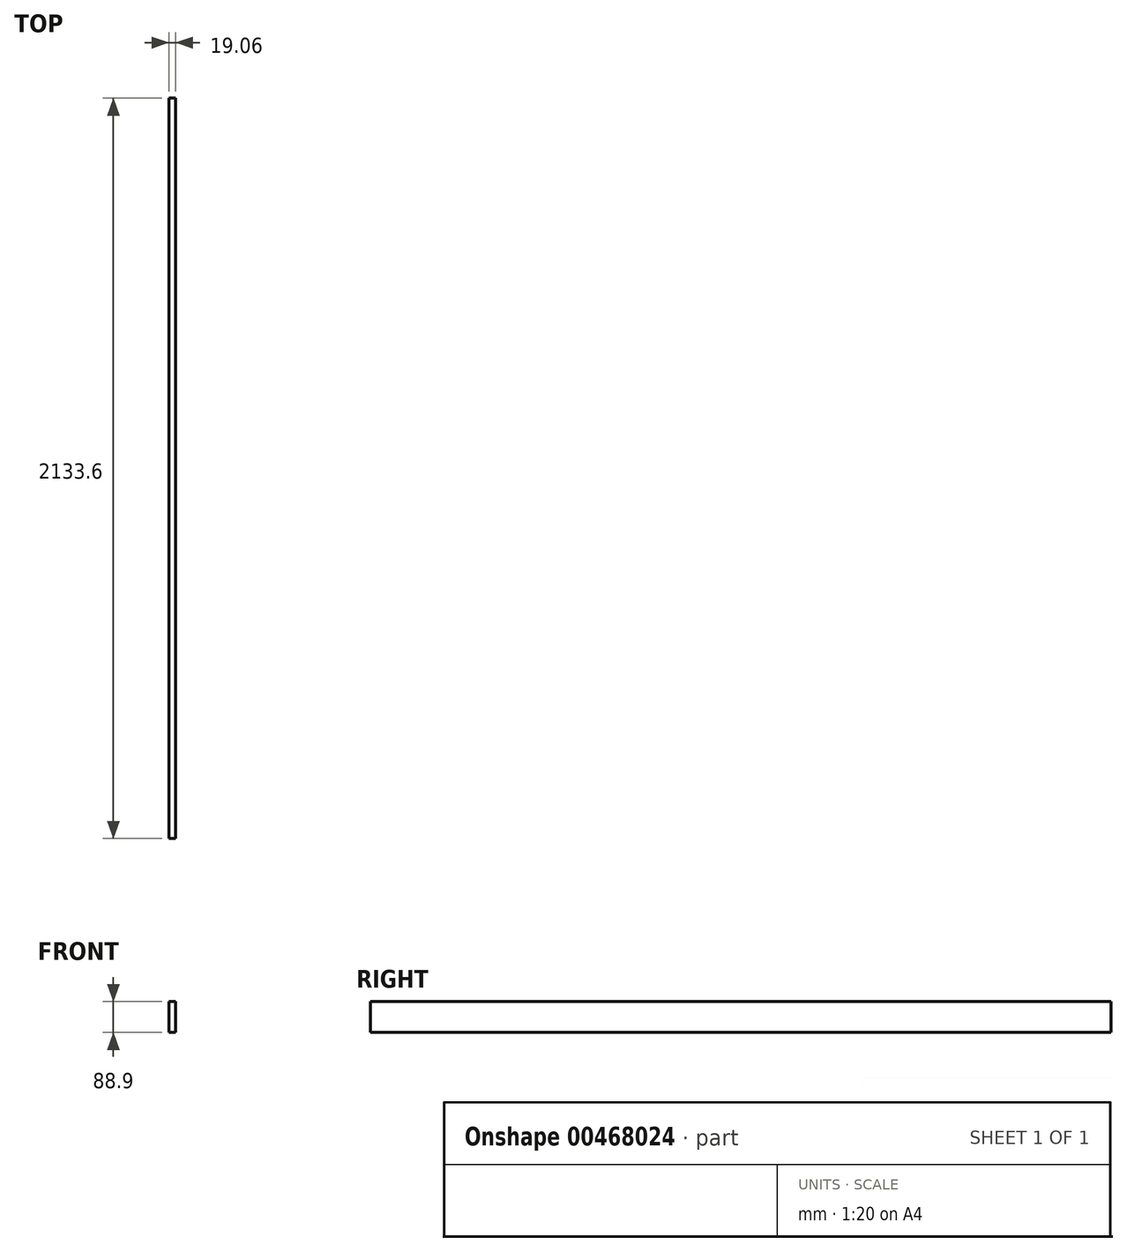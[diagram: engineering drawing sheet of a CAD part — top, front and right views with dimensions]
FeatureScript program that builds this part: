
annotation { "Feature Type Name" : "Feature", "Feature Type Description" : "" }
export const myFeature = defineFeature(function(context is Context, id is Id, definition is map)
    precondition{}
    {
        {
            var Q0;
            Q0=qCreatedBy(makeId("Front.planeOp"),FACE);
            var sketch = newSketch(context, id + "F0", { "sketchPlane" : qUnion([Q0])});
            skLineSegment(sketch, "E0.bottom", {"start": v(-9.53, -44.45) * mm, "end": v(9.53, -44.45) * mm});
            skLineSegment(sketch, "E0.top", {"start": v(-9.53, 44.45) * mm, "end": v(9.53, 44.45) * mm});
            skLineSegment(sketch, "E0.left", {"start": v(-9.53, -44.45) * mm, "end": v(-9.53, 44.45) * mm});
            skLineSegment(sketch, "E0.right", {"start": v(9.53, -44.45) * mm, "end": v(9.52, 44.45) * mm});
            skSolve(sketch);
        }
        {
            var Q0;
            Q0=makeQuery(id+"F0.imprint","IMPRINT",FACE,{"disambiguationData":[TD([[makeQuery(id+"F0.imprint","IMPRINT",EDGE,{"derivedFrom":sQuery(id+"F0.wireOp",EDGE,"E0.bottom")}),1.0]])]});
            extrude(context, id + "F1", {"entities" : qUnion([Q0]), "oppositeDirection" : true, "depth" : 2133.6 * mm});
        }
    });
